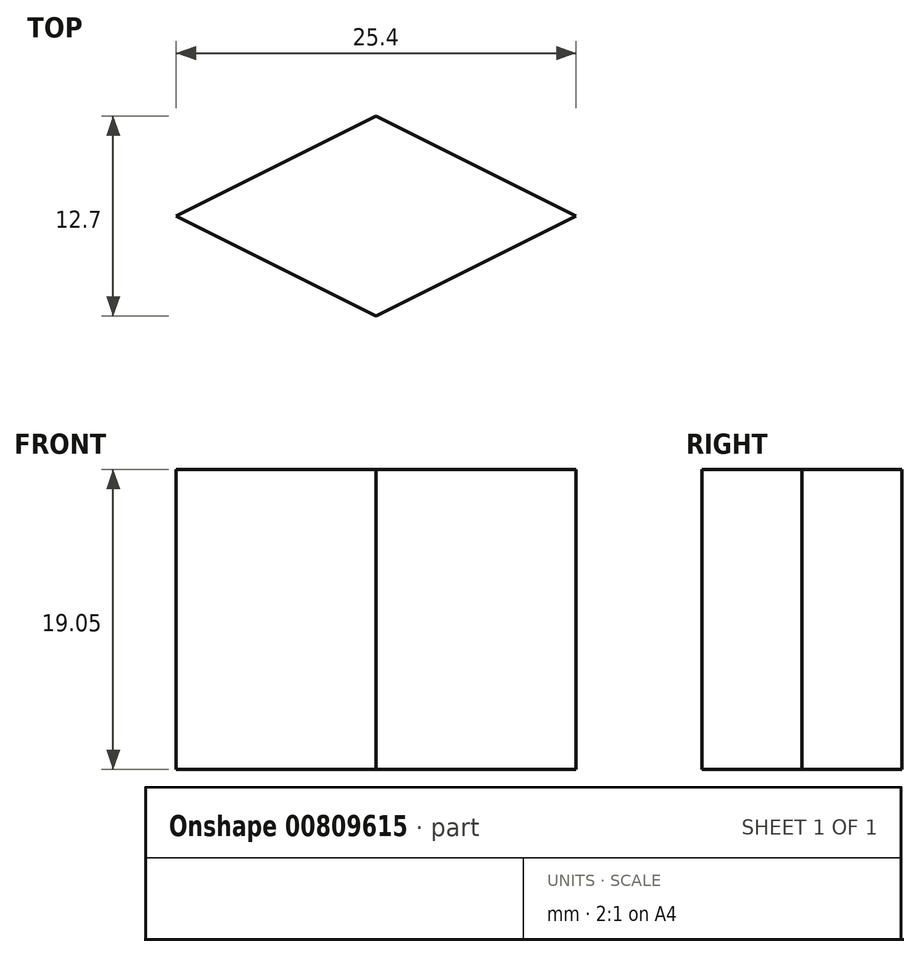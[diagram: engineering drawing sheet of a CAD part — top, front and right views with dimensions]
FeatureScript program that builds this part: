
annotation { "Feature Type Name" : "Feature", "Feature Type Description" : "" }
export const myFeature = defineFeature(function(context is Context, id is Id, definition is map)
    precondition{}
    {
        {
            var Q0;
            Q0=qCreatedBy(makeId("Top.planeOp"),FACE);
            var sketch = newSketch(context, id + "F0", { "sketchPlane" : qUnion([Q0])});
            skLineSegment(sketch, "E0", {"start": v(-12.7, 0) * mm, "end": v(0, 6.35) * mm});
            skLineSegment(sketch, "E1", {"start": v(0, 6.35) * mm, "end": v(12.7, 0) * mm});
            skLineSegment(sketch, "E2", {"start": v(12.7, 0) * mm, "end": v(0, -6.35) * mm});
            skLineSegment(sketch, "E3", {"start": v(0, -6.35) * mm, "end": v(-12.7, 0) * mm});
            skSolve(sketch);
        }
        {
            var Q0;
            Q0 = qSketchRegion(id + "F0", true);
            extrude(context, id + "F1", {"entities" : qUnion([Q0]), "depth" : 19.05 * mm, "offsetDistance" : 25.4 * mm});
        }
    });
